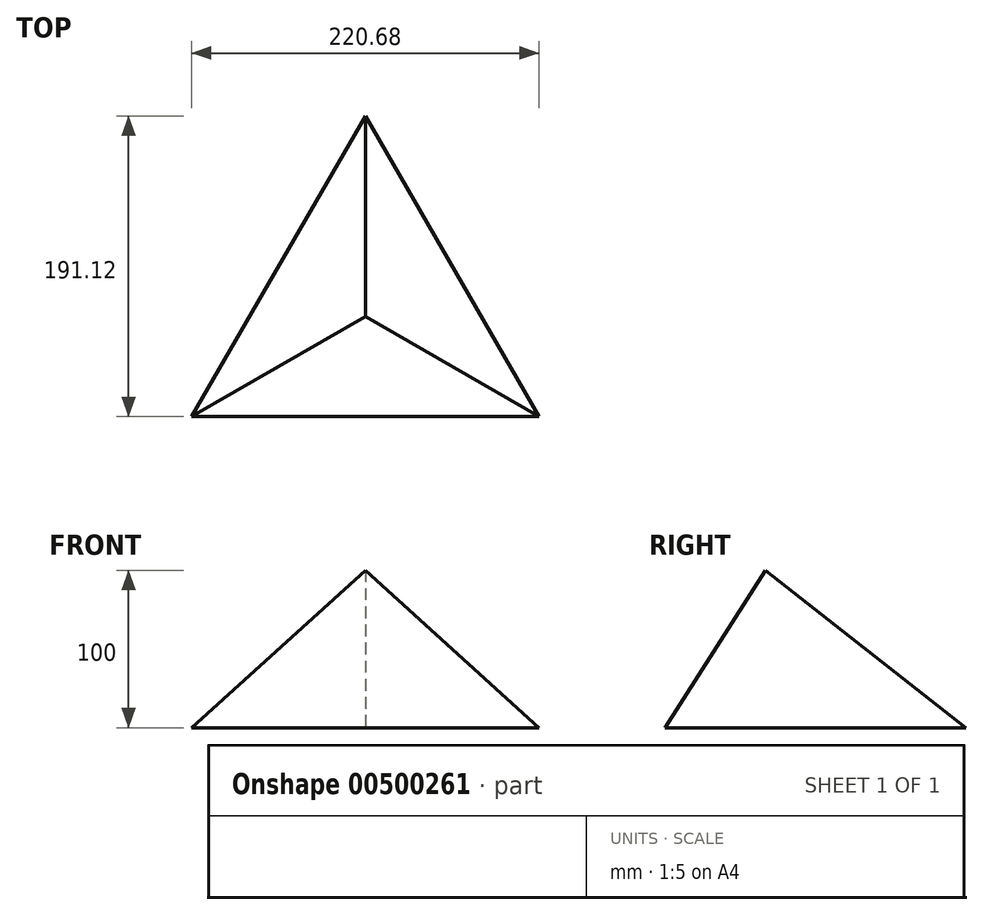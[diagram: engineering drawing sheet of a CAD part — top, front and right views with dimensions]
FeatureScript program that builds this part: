
annotation { "Feature Type Name" : "Feature", "Feature Type Description" : "" }
export const myFeature = defineFeature(function(context is Context, id is Id, definition is map)
    precondition{}
    {
        {
            var Q0;
            Q0=qCreatedBy(makeId("Top.planeOp"),FACE);
            var sketch = newSketch(context, id + "F0", { "sketchPlane" : qUnion([Q0])});
            skCircle(sketch, "E0.cCircle", {"center": v(0, 0) * mm, "radius": 127.41 * mm, "construction": true});
            skLineSegment(sketch, "E0.0", {"start": v(0, 127.41) * mm, "end": v(110.34, -63.7) * mm});
            skLineSegment(sketch, "E0.1", {"start": v(110.34, -63.7) * mm, "end": v(-110.34, -63.7) * mm});
            skLineSegment(sketch, "E0.2", {"start": v(-110.34, -63.7) * mm, "end": v(0, 127.41) * mm});
            skSolve(sketch);
        }
        {
            var Q0;
            Q0=qCreatedBy(makeId("Top.planeOp"),FACE);
            cPlane(context, id + "F1", {"entities" : qUnion([Q0]), "cplaneType" : CPlaneType.OFFSET, "offset" : 100 * mm, "width" : 150 * mm, "height" : 150 * mm});
        }
        {
            var Q0;
            Q0=qCreatedBy(id+"F1.planeOp",FACE);
            var sketch = newSketch(context, id + "F2", { "sketchPlane" : qUnion([Q0])});
            skPoint(sketch, "E1", {"position": v(0, 0) * mm});
            skSolve(sketch);
        }
        {
            var Q0;
            Q0=sQuery(id+"F2.wireOp",VERTEX,"E1");
            var Q1;
            Q1=makeQuery(id+"F0.imprint","IMPRINT",FACE,{"disambiguationData":[TD([[makeQuery(id+"F0.imprint","IMPRINT",EDGE,{"derivedFrom":sQuery(id+"F0.wireOp",EDGE,"E0.0")}),-1.0]])]});
            loft(context, id + "F3", {"sheetProfilesArray" : [{ "sheetProfileEntities" : qUnion([Q0]) }, { "sheetProfileEntities" : qUnion([Q1]) }]});
        }
    });
